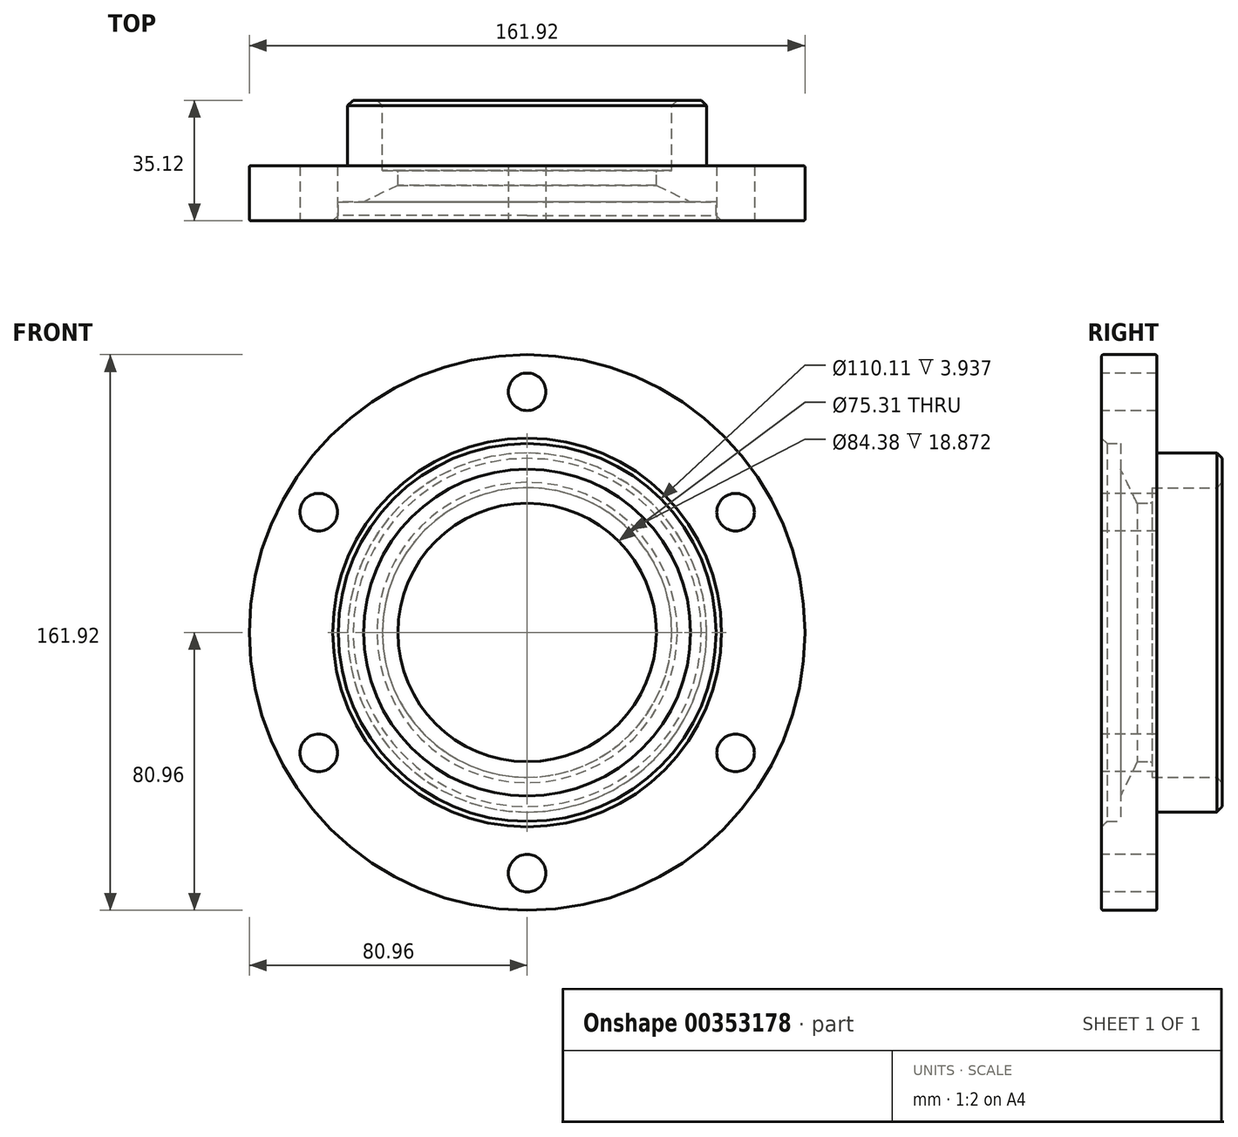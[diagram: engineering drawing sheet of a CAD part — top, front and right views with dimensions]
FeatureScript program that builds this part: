
annotation { "Feature Type Name" : "Feature", "Feature Type Description" : "" }
export const myFeature = defineFeature(function(context is Context, id is Id, definition is map)
    precondition{}
    {
        {
            var Q0;
            Q0=qCreatedBy(makeId("Right.planeOp"),FACE);
            var sketch = newSketch(context, id + "F0", { "sketchPlane" : qUnion([Q0])});
            skLineSegment(sketch, "E0", {"start": v(0, 80.96) * mm, "end": v(16.1, 80.96) * mm});
            skLineSegment(sketch, "E1", {"start": v(16.1, 80.96) * mm, "end": v(16.1, 52.31) * mm});
            skLineSegment(sketch, "E2", {"start": v(16.1, 52.31) * mm, "end": v(35.12, 52.31) * mm});
            skLineSegment(sketch, "E3", {"start": v(35.12, 52.31) * mm, "end": v(35.12, 0) * mm});
            skPoint(sketch, "E4.startSnap0", {"position": v(0, 40.48) * mm});
            skLineSegment(sketch, "E5", {"start": v(14.68, 37.66) * mm, "end": v(14.68, 42.19) * mm});
            skLineSegment(sketch, "E6", {"start": v(14.68, 42.19) * mm, "end": v(35.12, 42.19) * mm});
            skLineSegment(sketch, "E7", {"start": v(5.51, 55.05) * mm, "end": v(5.51, 47.63) * mm});
            skLineSegment(sketch, "E8", {"start": v(0, 80.96) * mm, "end": v(0, 55.05) * mm});
            skLineSegment(sketch, "E9", {"start": v(0, 55.05) * mm, "end": v(5.51, 55.05) * mm});
            skLineSegment(sketch, "E10", {"start": v(10.38, 37.66) * mm, "end": v(14.68, 37.66) * mm});
            skLineSegment(sketch, "E11", {"start": v(5.51, 47.63) * mm, "end": v(10.38, 37.66) * mm});
            skLineSegment(sketch, "E12", {"start": v(0, 55.05) * mm, "end": v(0, 0) * mm});
            skLineSegment(sketch, "E13", {"start": v(35.12, 0) * mm, "end": v(0, 0) * mm});
            skSolve(sketch);
        }
        {
            var Q0;
            Q0=makeQuery(id+"F0.imprint","IMPRINT",FACE,{"disambiguationData":[TD([[makeQuery(id+"F0.imprint","IMPRINT",EDGE,{"derivedFrom":sQuery(id+"F0.wireOp",EDGE,"E0")}),-1.0]])]});
            var Q1;
            Q1=sQuery(id+"F0.wireOp",EDGE,"E13");
            revolve(context, id + "F1", {"entities" : qUnion([Q0]), "axis" : qUnion([Q1]), "revolveType" : RevolveType.FULL});
        }
        {
            var Q0;
            Q0=makeQuery(id+"F1.opRevolve","SWEPT_EDGE",EDGE,{"disambiguationData":[OSD([sQuery(id+"F0.wireOp",EDGE,"E3"),sQuery(id+"F0.wireOp",EDGE,"E6")])]});
            var Q1;
            Q1=makeQuery(id+"F1.opRevolve","SWEPT_EDGE",EDGE,{"disambiguationData":[OSD([sQuery(id+"F0.wireOp",EDGE,"E2"),sQuery(id+"F0.wireOp",EDGE,"E3")])]});
            var Q2;
            Q2=makeQuery(id+"F1.opRevolve","SWEPT_EDGE",EDGE,{"disambiguationData":[OSD([sQuery(id+"F0.wireOp",EDGE,"E8"),sQuery(id+"F0.wireOp",EDGE,"E9")])]});
            chamfer(context, id + "F2", {"entities" : qUnion([Q0, Q1, Q2]), "width" : 1.57 * mm, "tangentPropagation" : true});
        }
        {
            var Q0;
            Q0=makeQuery(id+"F1.opRevolve","SWEPT_EDGE",EDGE,{"disambiguationData":[OSD([sQuery(id+"F0.wireOp",EDGE,"E5"),sQuery(id+"F0.wireOp",EDGE,"E10")])]});
            var Q1;
            Q1=makeQuery(id+"F1.opRevolve","SWEPT_EDGE",EDGE,{"disambiguationData":[OSD([sQuery(id+"F0.wireOp",EDGE,"E0"),sQuery(id+"F0.wireOp",EDGE,"E1")])]});
            var Q2;
            Q2=makeQuery(id+"F1.opRevolve","SWEPT_EDGE",EDGE,{"disambiguationData":[OSD([sQuery(id+"F0.wireOp",EDGE,"E0"),sQuery(id+"F0.wireOp",EDGE,"E8")])]});
            fillet(context, id + "F3", {"entities" : qUnion([Q0, Q1, Q2]), "radius" : 0.5 * mm, "tangentPropagation" : true, "allowEdgeOverflow" : false});
        }
        {
            var Q0;
            Q0=qCreatedBy(makeId("Front.planeOp"),FACE);
            var sketch = newSketch(context, id + "F4", { "sketchPlane" : qUnion([Q0])});
            skPoint(sketch, "E14", {"position": v(0, 70.14) * mm});
            skPoint(sketch, "E15.1.0", {"position": v(-60.74, 35.07) * mm});
            skPoint(sketch, "E15.2.0", {"position": v(-60.74, -35.07) * mm});
            skPoint(sketch, "E15.center", {"position": v(0, 0) * mm});
            skPoint(sketch, "E16.0.3.0", {"position": v(0, -70.14) * mm});
            skPoint(sketch, "E16.0.4.0", {"position": v(60.74, -35.07) * mm});
            skPoint(sketch, "E16.0.5.0", {"position": v(60.74, 35.07) * mm});
            skSolve(sketch);
        }
        {
            var Q0;
            Q0=sQuery(id+"F4.wireOp",VERTEX,"E14");
            var Q1;
            Q1=sQuery(id+"F4.wireOp",VERTEX,"E16.0.5.0");
            var Q2;
            Q2=sQuery(id+"F4.wireOp",VERTEX,"E16.0.4.0");
            var Q3;
            Q3=sQuery(id+"F4.wireOp",VERTEX,"E16.0.3.0");
            var Q4;
            Q4=sQuery(id+"F4.wireOp",VERTEX,"E15.2.0");
            var Q5;
            Q5=sQuery(id+"F4.wireOp",VERTEX,"E15.1.0");
            var Q6;
            Q6=makeQuery(id+"F1.opRevolve","SWEPT_BODY",BODY,{"disambiguationData":[OSD([sQuery(id+"F0.wireOp",EDGE,"E0"),sQuery(id+"F0.wireOp",EDGE,"E1"),sQuery(id+"F0.wireOp",EDGE,"E2"),sQuery(id+"F0.wireOp",EDGE,"E3"),sQuery(id+"F0.wireOp",EDGE,"E5"),sQuery(id+"F0.wireOp",EDGE,"E6"),sQuery(id+"F0.wireOp",EDGE,"E7"),sQuery(id+"F0.wireOp",EDGE,"E8"),sQuery(id+"F0.wireOp",EDGE,"E9"),sQuery(id+"F0.wireOp",EDGE,"E10"),sQuery(id+"F0.wireOp",EDGE,"E11")])]});
            hole(context, id + "F5", {"style" : HoleStyle.SIMPLE, "endStyle" : HoleEndStyle.THROUGH, "holeDiameter" : 10.95 * mm, "isTappedThrough" : true, "tappedDepth" : 12.7 * mm, "tapClearance" : 3, "locations" : qUnion([Q0, Q1, Q2, Q3, Q4, Q5]), "scope" : qUnion([Q6])});
        }
    });
